# Revit family: Hager-Univers-IP44-D205-H1400-Cl.II-Encl-NoHosted-PT-pt
name_source: partatom
category: Electrical Equipment
units: mm (PartAtom-declared; Revit-internal decimal feet)

## family parameters
Always vertical = Yes
Cut with Voids When Loaded = No
Panel Configuration = Two Columns, Circuits Across
Part Type = Panelboard
Room Calculation Point = No
Round Connector Dimension = Use Diameter
Shared = No
Work Plane-Based = Yes

## types (5) — shared parameters
Default Elevation = 1219 mm
EF000003 - Método de montagem = EV000384 - Montagem em superfície (gesso)
EF000007 - Cor = EV000202 - Branco
EF000040 - Altura = 1400 mm  [stored 4.59318 ft]
EF000049 - Profundidade = 205 mm  [stored 0.672572 ft]
EF000116 - Número RAL = 9010
EF000118 - Com tampa de montagem = No
EF000218 - Profundidade incorporada = 205 mm  [stored 0.672572 ft]
EF000266 - Número de linhas = 9
EF001088 - Extensão possível = Yes
EF001596 - Material do corpo = EV000179 - Aço
EF001613 - Integridade do circuito = EV000494 - Nenhum
EF003532 - Adequado para uso no exterior = No
EF004293 - Força de impacto = EV006815 - IK09
EF005474 - Grau de proteção (IP) = EV006418 - IP44
EF006244 - Tampa/porta transparente = No
EF006306 - Com fecho = No
EF007800 - Adequado para proteção contra raios = No
EF008873 - Corrente nominal (In) = 250 A
EF009170 - Espessura do material do invólucro = 1 mm  [stored 0.00328084 ft]
EF009171 - Espessura do material da porta/tampa = 1 mm  [stored 0.00328084 ft]
EF009212 - Tipo de tampa = EV000116 - Fechado
EF015940 - Tampa com libertação de sobrepressão = No
HG000002 - Com porta ou tampa = Yes
HG000003 - Gama = Univers
HG000006 - Encastrado = No
HG000023 - Recinto de secção dupla = No
HG000024 - Altura da secção inferior = 600 mm
HG000026 - Instalação no chão = No
Manufacturer = Hager
Type Comments = Univers
zero-valued in all types: HG000027 - Altura da Plinta

## per-type parameters (varying)
| type | EF000008 - Largura | EF000339 - Tipo de difusor | EF000437 - Número de entradas de condutores | EF001131 - Profundidade interior | EF002950 - Largura em número de módulos | EF004427 - Número de módulos | EF004464 - Tipo de porta | EF009554 - Número de aberturas para placas de flange | HG000004 - Referência do Fabricante | HG000009 - Porta dupla | HG000010 - Portas assimétricas |
| Montagem em superfície (gesso) IP44 L1050 A1400 P205  - FP94SN2 | 1050 mm | EV001012 - Tampa | 8 | 143 mm | 48 | 432 | EV003602 - Duplo | 8 | FP94SN2 | Yes | No |
| Montagem em superfície (gesso) IP44 L1300 A1400 P205  - FP95SN2 | 1300 mm  [stored 4.26509 ft] | EV004216 - Porta | 10 | 130 mm  [stored 0.426509 ft] | 60 | 540 | EV003602 - Duplo | 10 | FP95SN2 | Yes | Yes |
| Montagem em superfície (gesso) IP44 L300 A1400 P205  - FP91SN2 | 300 mm | EV001012 - Tampa | 2 | 143 mm | 12 | 108 | EV002646 - Único | 2 | FP91SN2 | No | No |
| Montagem em superfície (gesso) IP44 L550 A1400 P205  - FP92SN2 | 550 mm | EV001012 - Tampa | 4 | 143 mm | 24 | 216 | EV002646 - Único | 4 | FP92SN2 | No | No |
| Montagem em superfície (gesso) IP44 L800 A1400 P205  - FP93SN2 | 800 mm  [stored 2.62467 ft] | EV001012 - Tampa | 6 | 143 mm | 36 | 324 | EV002646 - Único | 6 | FP93SN2 | No | No |

note: [stored X ft] marks values corroborated as IEEE doubles in the binary element streams (Revit-internal decimal feet)

## geometry (parser evidence)
native form markers: Blend x4, Sweep x11
no freeform markers — native parametric forms only
